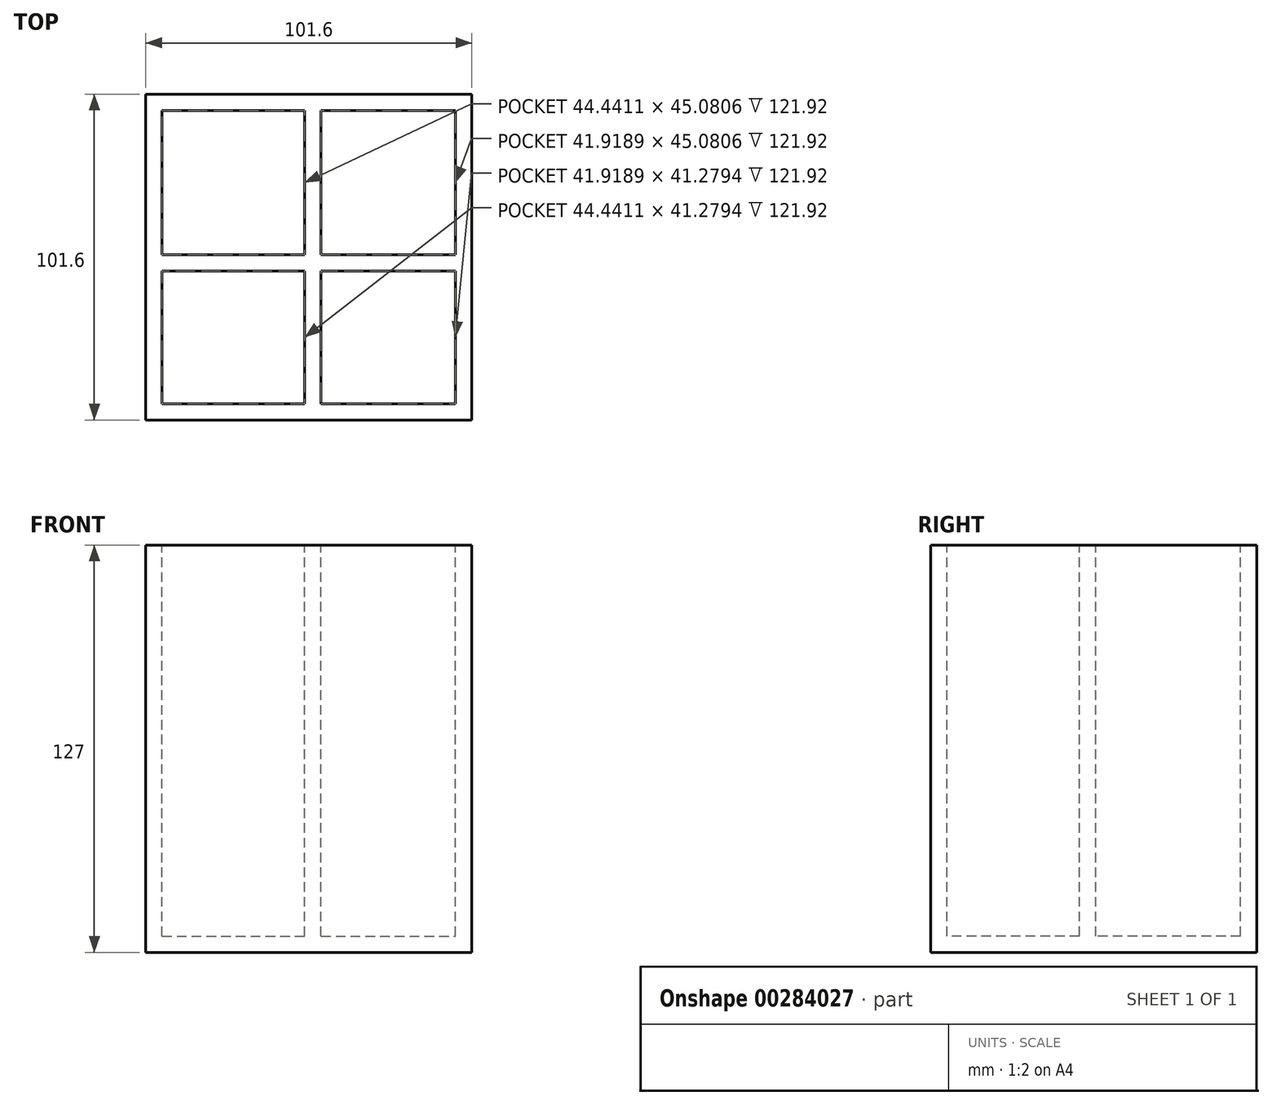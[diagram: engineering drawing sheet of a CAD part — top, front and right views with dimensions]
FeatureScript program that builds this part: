
annotation { "Feature Type Name" : "Feature", "Feature Type Description" : "" }
export const myFeature = defineFeature(function(context is Context, id is Id, definition is map)
    precondition{}
    {
        {
            var Q0;
            Q0=qCreatedBy(makeId("Top.planeOp"),FACE);
            var sketch = newSketch(context, id + "F0", { "sketchPlane" : qUnion([Q0])});
            skLineSegment(sketch, "E0.bottom", {"start": v(50.8, 50.8) * mm, "end": v(-50.8, 50.8) * mm});
            skLineSegment(sketch, "E0.top", {"start": v(50.8, -50.8) * mm, "end": v(-50.8, -50.8) * mm});
            skLineSegment(sketch, "E0.left", {"start": v(50.8, 50.8) * mm, "end": v(50.8, -50.8) * mm});
            skLineSegment(sketch, "E0.right", {"start": v(-50.8, 50.8) * mm, "end": v(-50.8, -50.8) * mm});
            skPoint(sketch, "E0.middle", {"position": v(0, 0) * mm});
            skSolve(sketch);
        }
        {
            var Q0;
            Q0 = qSketchRegion(id + "F0", true);
            extrude(context, id + "F1", {"entities" : qUnion([Q0]), "depth" : 127 * mm});
        }
        {
            var Q0;
            Q0=makeQuery(id+"F1.opExtrude","CAP_FACE",FACE,{"disambiguationData":[OSD([sQuery(id+"F0.wireOp",EDGE,"E0.bottom"),sQuery(id+"F0.wireOp",EDGE,"E0.top"),sQuery(id+"F0.wireOp",EDGE,"E0.left"),sQuery(id+"F0.wireOp",EDGE,"E0.right")])],"isStart":false});
            var sketch = newSketch(context, id + "F2", { "sketchPlane" : qUnion([Q0])});
            skLineSegment(sketch, "E1.bottom", {"start": v(-45.72, 45.72) * mm, "end": v(-1.28, 45.72) * mm});
            skLineSegment(sketch, "E1.top", {"start": v(-45.72, 0.64) * mm, "end": v(-1.28, 0.64) * mm});
            skLineSegment(sketch, "E1.left", {"start": v(-45.72, 45.72) * mm, "end": v(-45.72, 0.64) * mm});
            skLineSegment(sketch, "E1.right", {"start": v(-1.28, 45.72) * mm, "end": v(-1.28, 0.64) * mm});
            skLineSegment(sketch, "E2.bottom", {"start": v(3.8, 0.64) * mm, "end": v(45.72, 0.64) * mm});
            skLineSegment(sketch, "E2.top", {"start": v(3.8, 45.72) * mm, "end": v(45.72, 45.72) * mm});
            skLineSegment(sketch, "E2.left", {"start": v(3.8, 0.64) * mm, "end": v(3.8, 45.72) * mm});
            skLineSegment(sketch, "E2.right", {"start": v(45.72, 0.64) * mm, "end": v(45.72, 45.72) * mm});
            skLineSegment(sketch, "E3.bottom", {"start": v(3.8, -4.44) * mm, "end": v(45.72, -4.44) * mm});
            skLineSegment(sketch, "E3.top", {"start": v(3.8, -45.72) * mm, "end": v(45.72, -45.72) * mm});
            skLineSegment(sketch, "E3.left", {"start": v(3.8, -4.44) * mm, "end": v(3.8, -45.72) * mm});
            skLineSegment(sketch, "E3.right", {"start": v(45.72, -4.44) * mm, "end": v(45.72, -45.72) * mm});
            skLineSegment(sketch, "E4.bottom", {"start": v(-1.28, -4.44) * mm, "end": v(-45.72, -4.44) * mm});
            skLineSegment(sketch, "E4.top", {"start": v(-1.28, -45.72) * mm, "end": v(-45.72, -45.72) * mm});
            skLineSegment(sketch, "E4.left", {"start": v(-1.28, -4.44) * mm, "end": v(-1.28, -45.72) * mm});
            skLineSegment(sketch, "E4.right", {"start": v(-45.72, -4.44) * mm, "end": v(-45.72, -45.72) * mm});
            skSolve(sketch);
        }
        {
            var Q0;
            Q0 = qSketchRegion(id + "F2", true);
            extrude(context, id + "F3", {"entities" : qUnion([Q0]), "operationType" : NewBodyOperationType.REMOVE, "oppositeDirection" : true, "depth" : 121.92 * mm});
        }
    });
